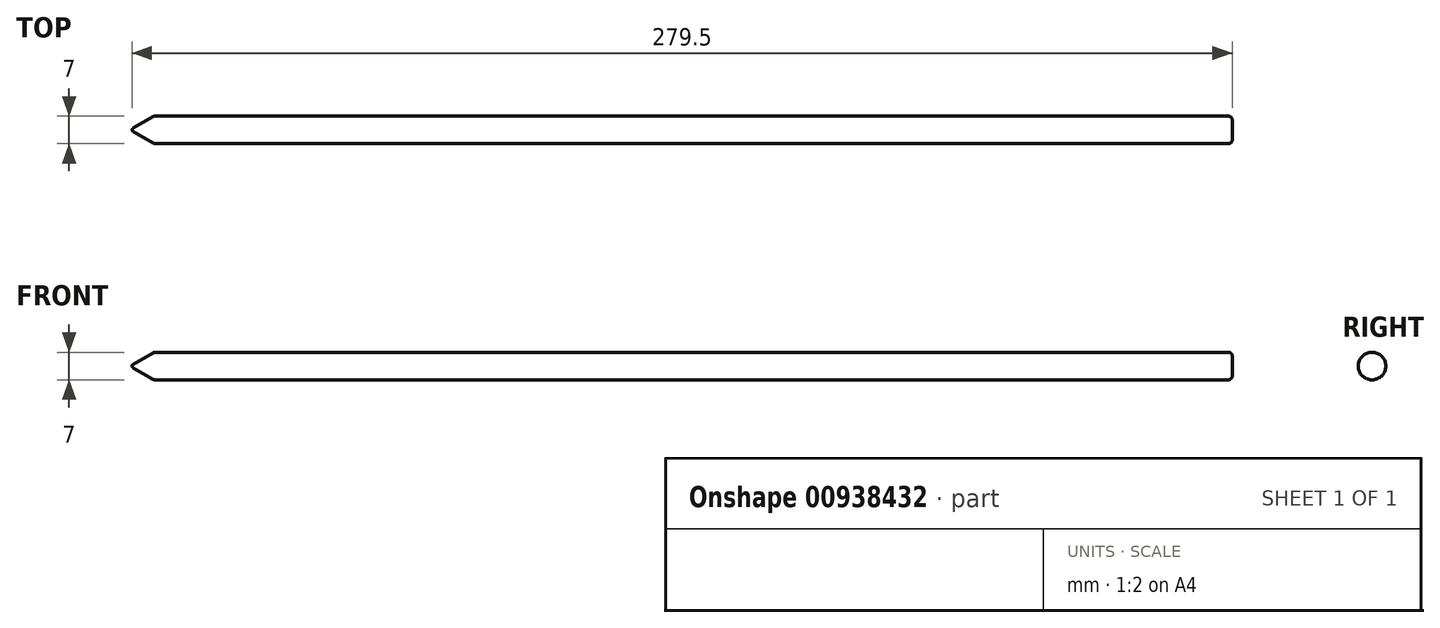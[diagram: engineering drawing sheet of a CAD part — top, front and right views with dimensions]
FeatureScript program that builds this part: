
annotation { "Feature Type Name" : "Feature", "Feature Type Description" : "" }
export const myFeature = defineFeature(function(context is Context, id is Id, definition is map)
    precondition{}
    {
        {
            var Q0;
            Q0=qCreatedBy(makeId("Top.planeOp"),FACE);
            var sketch = newSketch(context, id + "F0", { "sketchPlane" : qUnion([Q0])});
            skLineSegment(sketch, "E0", {"start": v(-280, 0) * mm, "end": v(-274.17, -3.37) * mm});
            skLineSegment(sketch, "E1", {"start": v(-273.67, -3.5) * mm, "end": v(-1, -3.5) * mm});
            skLineSegment(sketch, "E2", {"start": v(0, -2.5) * mm, "end": v(0, 0) * mm});
            skLineSegment(sketch, "E3", {"start": v(0, 0) * mm, "end": v(-280, 0) * mm});
            skPoint(sketch, "E4.visualSharp", {"position": v(-273.94, -3.5) * mm});
            skArc(sketch, "E4.filletArc", {"start": v(-274.17, -3.37) * mm, "mid": v(-273.93, -3.47) * mm, "end": v(-273.67, -3.5) * mm});
            skArc(sketch, "E5", {"start": v(-279.5, 0) * mm, "mid": v(-279.43, -0.25) * mm, "end": v(-279.25, -0.43) * mm});
            skLineSegment(sketch, "E6", {"start": v(-279.5, 0) * mm, "end": v(-279.5, 0.32) * mm});
            skPoint(sketch, "E7.visualSharp", {"position": v(0, -3.5) * mm});
            skArc(sketch, "E7.filletArc", {"start": v(-1, -3.5) * mm, "mid": v(-0.3, -3.2) * mm, "end": v(0, -2.5) * mm});
            skSolve(sketch);
        }
        {
            var Q0;
            Q0=makeQuery(id+"F0.imprint","IMPRINT",FACE,{"disambiguationData":[TD([[makeQuery(id+"F0.imprint","IMPRINT",EDGE,{"derivedFrom":sQuery(id+"F0.wireOp",EDGE,"E1")}),1.0]])]});
            var Q1;
            Q1=sQuery(id+"F0.wireOp",EDGE,"E3");
            revolve(context, id + "F1", {"surfaceOperationType" : NewSurfaceOperationType.NEW, "entities" : qUnion([Q0]), "axis" : qUnion([Q1]), "revolveType" : RevolveType.FULL});
        }
    });
